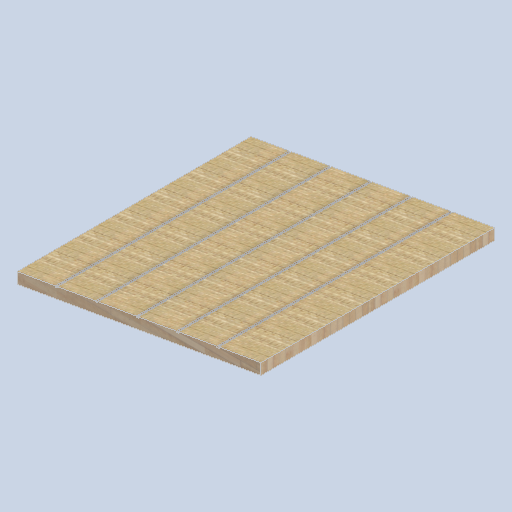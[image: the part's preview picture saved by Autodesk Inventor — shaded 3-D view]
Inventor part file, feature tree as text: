
AUTODESK INVENTOR PART (.ipt)
format: ipt  version: 2024.2 (Build 282272000, 272)  size: 428,544 bytes
history: native  units: mm
features: sketch x4, plane x3, extrude x2
ambient origin geometry x8: Origin, YZ Plane, XZ Plane, XY Plane, X Axis, Y Axis, Z Axis, Center Point
bodies: Solid1 (feature_tree)
feature tree (9):
  sketch  "Sketch1"  dims[d0=100.0mm d1=2110.0mm]
  plane  "Work Plane2"
  sketch  "Sketch2"  dims[d2=2200.0mm d3=13.962634mm]
  plane  "Work Plane3"
  extrude  "Extrusion1"  Depth=2110.0mm
  extrude  "Extrusion2"  Depth=2200.0mm
  plane  "Work Plane1"
  sketch  "Sketch3"  dims[d4=13.962634mm]
  sketch  "Sketch4"  dims[d5=2110.0mm d6=0.0mm d7=350.0mm d8=350.0mm d9=350.0mm d10=350.0mm d11=350.0mm d12=0.0mm d13=0.0mm]
